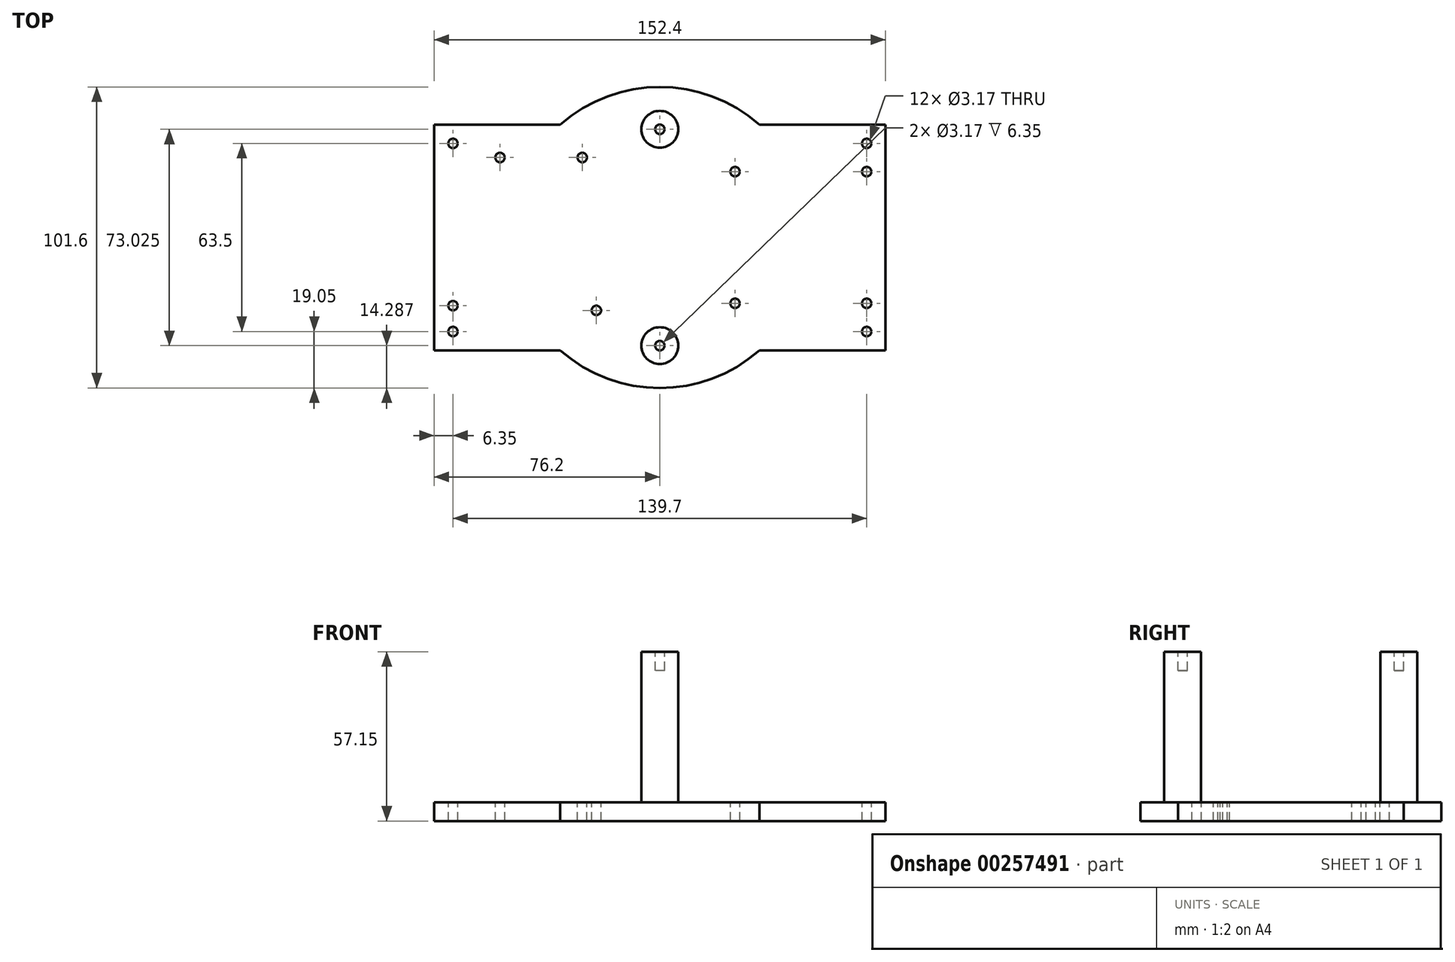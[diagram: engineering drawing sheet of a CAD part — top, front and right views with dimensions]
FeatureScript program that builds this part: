
annotation { "Feature Type Name" : "Feature", "Feature Type Description" : "" }
export const myFeature = defineFeature(function(context is Context, id is Id, definition is map)
    precondition{}
    {
        {
            var Q0;
            Q0=qCreatedBy(makeId("Top.planeOp"),FACE);
            var sketch = newSketch(context, id + "F0", { "sketchPlane" : qUnion([Q0])});
            skCircle(sketch, "E0", {"center": v(0, 0) * mm, "radius": 50.8 * mm});
            skSolve(sketch);
        }
        {
            var Q0;
            Q0 = qSketchRegion(id + "F0", true);
            extrude(context, id + "F1", {"entities" : qUnion([Q0]), "depth" : 6.35 * mm});
        }
        {
            var Q0;
            Q0=makeQuery(id+"F1.opExtrude","CAP_FACE",FACE,{"disambiguationData":[OSD([sQuery(id+"F0.wireOp",EDGE,"E0")])],"isStart":false});
            var sketch = newSketch(context, id + "F2", { "sketchPlane" : qUnion([Q0])});
            skCircle(sketch, "E1", {"center": v(0, -36.51) * mm, "radius": 6.22 * mm});
            skCircle(sketch, "E2.MirrorC", {"center": v(0, 36.51) * mm, "radius": 6.22 * mm});
            skSolve(sketch);
        }
        {
            var Q0;
            Q0 = qSketchRegion(id + "F2", true);
            extrude(context, id + "F3", {"entities" : qUnion([Q0]), "operationType" : NewBodyOperationType.ADD, "depth" : 50.8 * mm});
        }
        {
            var Q0;
            Q0=qCreatedBy(makeId("Top.planeOp"),FACE);
            var sketch = newSketch(context, id + "F4", { "sketchPlane" : qUnion([Q0])});
            skLineSegment(sketch, "E3.bottom", {"start": v(76.2, -38.1) * mm, "end": v(-76.2, -38.1) * mm});
            skLineSegment(sketch, "E3.top", {"start": v(76.2, 38.1) * mm, "end": v(-76.2, 38.1) * mm});
            skLineSegment(sketch, "E3.left", {"start": v(76.2, -38.1) * mm, "end": v(76.2, 38.1) * mm});
            skLineSegment(sketch, "E3.right", {"start": v(-76.2, -38.1) * mm, "end": v(-76.2, 38.1) * mm});
            skPoint(sketch, "E3.middle", {"position": v(0, 0) * mm});
            skSolve(sketch);
        }
        {
            var Q0;
            Q0 = qSketchRegion(id + "F4", true);
            extrude(context, id + "F5", {"entities" : qUnion([Q0]), "operationType" : NewBodyOperationType.ADD, "depth" : 6.35 * mm});
        }
        {
            var Q0;
            {var subQ0=sQuery(id+"F0.wireOp",EDGE,"E0");Q0=makeQuery(id+"F5.boolean.opBoolean","MERGE",FACE,{"derivedFrom":[makeQuery(id+"Fb6f5BAOOv0yVDo_1.boolean.opBoolean","SPLIT",FACE,{"disambiguationData":[TD([makeQuery(id+"F1.opExtrude","SWEPT_FACE",FACE,{"disambiguationData":[OSD([subQ0])]})])],"derivedFrom":makeQuery(id+"F1.opExtrude","CAP_FACE",FACE,{"disambiguationData":[OSD([subQ0])],"isStart":false})}),makeQuery(id+"F5.opExtrude","CAP_FACE",FACE,{"disambiguationData":[OSD([sQuery(id+"F4.wireOp",EDGE,"E3.bottom"),sQuery(id+"F4.wireOp",EDGE,"E3.top"),sQuery(id+"F4.wireOp",EDGE,"E3.left"),sQuery(id+"F4.wireOp",EDGE,"E3.right")])],"isStart":false})]});}
            var sketch = newSketch(context, id + "F6", { "sketchPlane" : qUnion([Q0])});
            skCircle(sketch, "E4", {"center": v(-53.98, 26.99) * mm, "radius": 1.59 * mm});
            skCircle(sketch, "E5", {"center": v(-69.85, -23.02) * mm, "radius": 1.59 * mm});
            skCircle(sketch, "E6", {"center": v(-26.2, 26.99) * mm, "radius": 1.59 * mm});
            skCircle(sketch, "E7", {"center": v(-21.43, -24.6) * mm, "radius": 1.59 * mm});
            skCircle(sketch, "E8", {"center": v(25.4, 22.22) * mm, "radius": 1.59 * mm});
            skCircle(sketch, "E9", {"center": v(69.85, 22.23) * mm, "radius": 1.59 * mm});
            skCircle(sketch, "E10", {"center": v(25.4, -22.23) * mm, "radius": 1.59 * mm});
            skCircle(sketch, "E11", {"center": v(69.85, -22.23) * mm, "radius": 1.59 * mm});
            skSolve(sketch);
        }
        {
            var Q0;
            Q0 = qSketchRegion(id + "F6", true);
            extrude(context, id + "F7", {"entities" : qUnion([Q0]), "operationType" : NewBodyOperationType.REMOVE, "endBound" : BoundingType.UP_TO_NEXT, "oppositeDirection" : true, "depth" : 25.4 * mm});
        }
        {
            var Q0;
            Q0=makeQuery(id+"F3.opExtrude","CAP_FACE",FACE,{"disambiguationData":[OSD([sQuery(id+"F2.wireOp",EDGE,"E2.MirrorC")])],"isStart":false});
            var sketch = newSketch(context, id + "F8", { "sketchPlane" : qUnion([Q0])});
            skCircle(sketch, "E12", {"center": v(0, 36.51) * mm, "radius": 1.59 * mm});
            skCircle(sketch, "E13", {"center": v(0, -36.51) * mm, "radius": 1.59 * mm});
            skSolve(sketch);
        }
        {
            var Q0;
            Q0 = qSketchRegion(id + "F8", true);
            extrude(context, id + "F9", {"entities" : qUnion([Q0]), "operationType" : NewBodyOperationType.REMOVE, "oppositeDirection" : true, "depth" : 6.35 * mm});
        }
        {
            var Q0;
            {var subQ0=sQuery(id+"F0.wireOp",EDGE,"E0");Q0=makeQuery(id+"F5.boolean.opBoolean","MERGE",FACE,{"derivedFrom":[makeQuery(id+"Fb6f5BAOOv0yVDo_1.boolean.opBoolean","SPLIT",FACE,{"disambiguationData":[TD([makeQuery(id+"F1.opExtrude","SWEPT_FACE",FACE,{"disambiguationData":[OSD([subQ0])]})])],"derivedFrom":makeQuery(id+"F1.opExtrude","CAP_FACE",FACE,{"disambiguationData":[OSD([subQ0])],"isStart":false})}),makeQuery(id+"F5.opExtrude","CAP_FACE",FACE,{"disambiguationData":[OSD([sQuery(id+"F4.wireOp",EDGE,"E3.bottom"),sQuery(id+"F4.wireOp",EDGE,"E3.top"),sQuery(id+"F4.wireOp",EDGE,"E3.left"),sQuery(id+"F4.wireOp",EDGE,"E3.right")])],"isStart":false})]});}
            var sketch = newSketch(context, id + "F10", { "sketchPlane" : qUnion([Q0])});
            skCircle(sketch, "E14", {"center": v(-69.85, 31.75) * mm, "radius": 1.59 * mm});
            skCircle(sketch, "E15", {"center": v(-69.85, -31.75) * mm, "radius": 1.59 * mm});
            skCircle(sketch, "E16", {"center": v(69.85, -31.75) * mm, "radius": 1.59 * mm});
            skCircle(sketch, "E17", {"center": v(69.85, 31.75) * mm, "radius": 1.59 * mm});
            skSolve(sketch);
        }
        {
            var Q0;
            Q0 = qSketchRegion(id + "F10", true);
            extrude(context, id + "F11", {"entities" : qUnion([Q0]), "operationType" : NewBodyOperationType.REMOVE, "oppositeDirection" : true, "depth" : 25.4 * mm});
        }
    });
